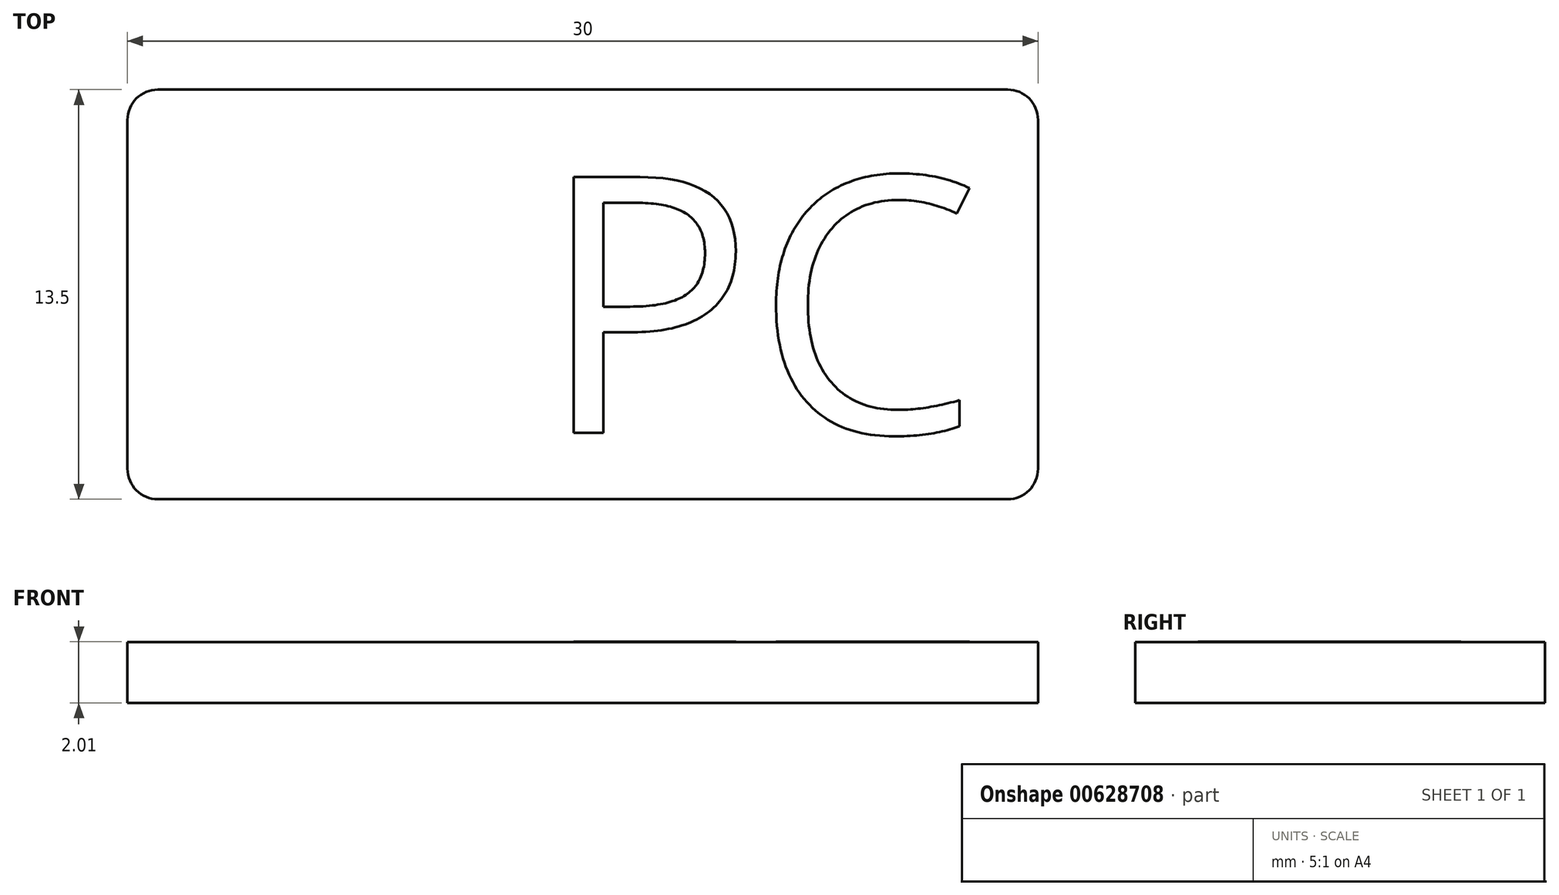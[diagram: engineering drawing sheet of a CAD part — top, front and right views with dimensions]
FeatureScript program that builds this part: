
annotation { "Feature Type Name" : "Feature", "Feature Type Description" : "" }
export const myFeature = defineFeature(function(context is Context, id is Id, definition is map)
    precondition{}
    {
        {
            var Q0;
            Q0=qCreatedBy(makeId("Top.planeOp"),FACE);
            var sketch = newSketch(context, id + "F0", { "sketchPlane" : qUnion([Q0])});
            skLineSegment(sketch, "E0.bottom", {"start": v(14, 6.75) * mm, "end": v(-14, 6.75) * mm});
            skLineSegment(sketch, "E0.top", {"start": v(14, -6.75) * mm, "end": v(-14, -6.75) * mm});
            skLineSegment(sketch, "E0.left", {"start": v(15, 5.75) * mm, "end": v(15, -5.75) * mm});
            skLineSegment(sketch, "E0.right", {"start": v(-15, 5.75) * mm, "end": v(-15, -5.75) * mm});
            skPoint(sketch, "E0.middle", {"position": v(0, 0) * mm});
            skPoint(sketch, "E1.visualSharp", {"position": v(-15, 6.75) * mm});
            skArc(sketch, "E1.filletArc", {"start": v(-14, 6.75) * mm, "mid": v(-14.7, 6.46) * mm, "end": v(-15, 5.75) * mm});
            skPoint(sketch, "E2.visualSharp", {"position": v(15, 6.75) * mm});
            skArc(sketch, "E2.filletArc", {"start": v(15, 5.75) * mm, "mid": v(14.7, 6.46) * mm, "end": v(14, 6.75) * mm});
            skPoint(sketch, "E3.visualSharp", {"position": v(15, -6.75) * mm});
            skArc(sketch, "E3.filletArc", {"start": v(14, -6.75) * mm, "mid": v(14.7, -6.46) * mm, "end": v(15, -5.75) * mm});
            skPoint(sketch, "E4.visualSharp", {"position": v(-15, -6.75) * mm});
            skArc(sketch, "E4.filletArc", {"start": v(-15, -5.75) * mm, "mid": v(-14.7, -6.46) * mm, "end": v(-14, -6.75) * mm});
            skSolve(sketch);
        }
        {
            var Q0;
            Q0 = qSketchRegion(id + "F0", true);
            extrude(context, id + "F1", {"entities" : qUnion([Q0]), "endBound" : BoundingType.SYMMETRIC, "depth" : 2 * mm, "offsetDistance" : 25 * mm});
        }
        {
            var Q0;
            Q0=makeQuery(id+"F1.opExtrude","CAP_FACE",FACE,{"disambiguationData":[OSD([sQuery(id+"F0.wireOp",EDGE,"E0.bottom"),sQuery(id+"F0.wireOp",EDGE,"E0.top"),sQuery(id+"F0.wireOp",EDGE,"E0.left"),sQuery(id+"F0.wireOp",EDGE,"E0.right"),sQuery(id+"F0.wireOp",EDGE,"E1.filletArc"),sQuery(id+"F0.wireOp",EDGE,"E2.filletArc"),sQuery(id+"F0.wireOp",EDGE,"E3.filletArc"),sQuery(id+"F0.wireOp",EDGE,"E4.filletArc")])],"isStart":false});
            var sketch = newSketch(context, id + "F2", { "sketchPlane" : qUnion([Q0])});
            skText(sketch, "E5", { "text": "PC", "fontName": "OpenSans-Regular.ttf"});
            const initialGuessF2  = {"E5": [-0.00146, -0.00456, 1, 0, 0.0085]};
            skSetInitialGuess(sketch, initialGuessF2);
            skSolve(sketch);
        }
        {
            var Q0;
            Q0 = qSketchRegion(id + "F2", true);
            extrude(context, id + "F3", {"entities" : qUnion([Q0]), "operationType" : NewBodyOperationType.ADD, "depth" : 0.01 * mm, "offsetDistance" : 25 * mm});
        }
    });
